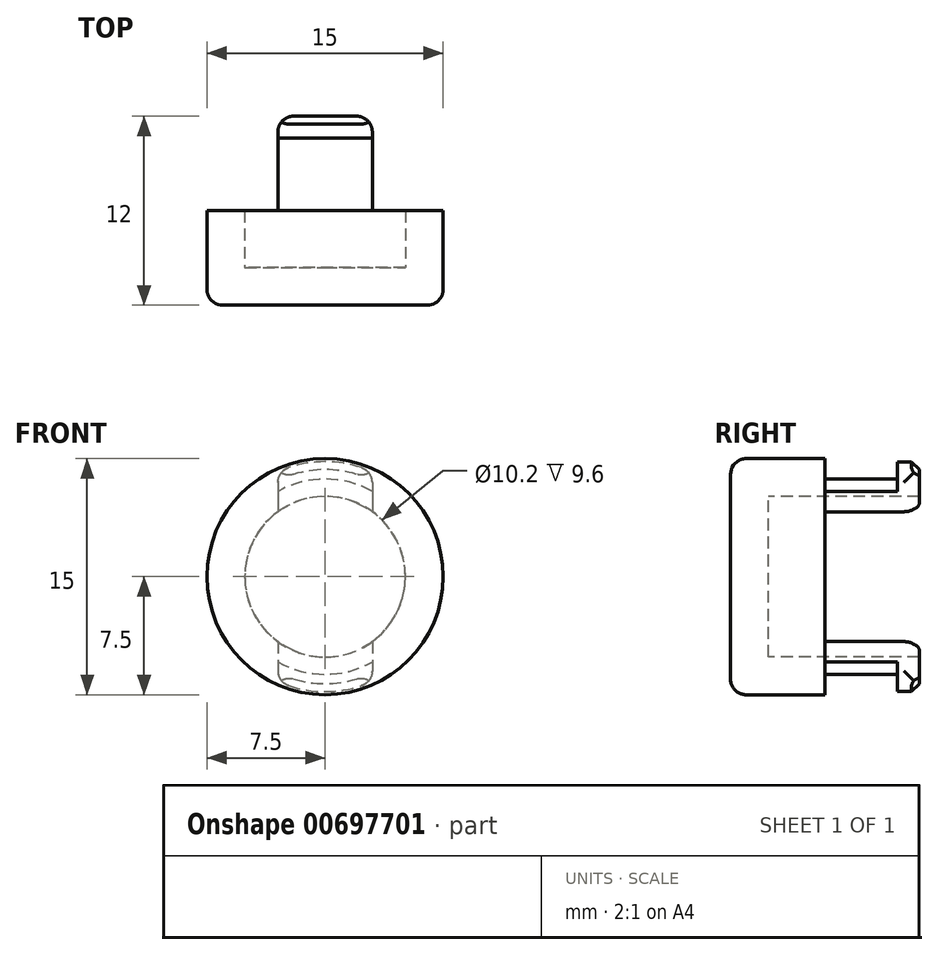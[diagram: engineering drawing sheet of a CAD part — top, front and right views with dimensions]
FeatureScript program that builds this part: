
annotation { "Feature Type Name" : "Feature", "Feature Type Description" : "" }
export const myFeature = defineFeature(function(context is Context, id is Id, definition is map)
    precondition{}
    {
        {
            var Q0;
            Q0=qCreatedBy(makeId("Front.planeOp"),FACE);
            cPlane(context, id + "F0", {"entities" : qUnion([Q0]), "cplaneType" : CPlaneType.OFFSET, "offset" : 13 * mm, "width" : 150 * mm, "height" : 150 * mm});
        }
        {
            var Q0;
            Q0=qCreatedBy(id+"F0.planeOp",FACE);
            var sketch = newSketch(context, id + "F1", { "sketchPlane" : qUnion([Q0])});
            skCircle(sketch, "E0", {"center": v(-13, 13) * mm, "radius": 7.5 * mm});
            skSolve(sketch);
        }
        {
            var Q0;
            Q0 = qSketchRegion(id + "F1", true);
            extrude(context, id + "F2", {"entities" : qUnion([Q0]), "oppositeDirection" : true, "depth" : 6 * mm, "offsetDistance" : 25 * mm});
        }
        {
            var Q0;
            Q0=makeQuery(id+"F2.opExtrude","CAP_EDGE",EDGE,{"disambiguationData":[OSD([sQuery(id+"F1.wireOp",EDGE,"E0")])],"isStart":true});
            fillet(context, id + "F3", {"entities" : qUnion([Q0]), "radius" : 1 * mm, "tangentPropagation" : true, "allowEdgeOverflow" : false});
        }
        {
            var Q0;
            Q0=makeQuery(id+"F2.opExtrude","CAP_FACE",FACE,{"disambiguationData":[OSD([sQuery(id+"F1.wireOp",EDGE,"E0")])],"isStart":false});
            shell(context, id + "F4", {"entities" : qUnion([Q0]), "thickness" : 2.4 * mm});
        }
        {
            var Q0;
            Q0=qCreatedBy(makeId("Front.planeOp"),FACE);
            cPlane(context, id + "F5", {"entities" : qUnion([Q0]), "cplaneType" : CPlaneType.OFFSET, "offset" : 2.4 * mm, "width" : 150 * mm, "height" : 150 * mm});
        }
        {
            var Q0;
            Q0=qCreatedBy(id+"F5.planeOp",FACE);
            var sketch = newSketch(context, id + "F6", { "sketchPlane" : qUnion([Q0])});
            skLineSegment(sketch, "E1.left", {"start": v(-10, 18.43) * mm, "end": v(-10, 17.12) * mm});
            skLineSegment(sketch, "E1.right", {"start": v(-16, 18.43) * mm, "end": v(-16, 17.12) * mm});
            skLineSegment(sketch, "E2.trimOffspring", {"start": v(-16, 8.88) * mm, "end": v(-16, 7.57) * mm});
            skLineSegment(sketch, "E3.trimOffspring", {"start": v(-10, 8.88) * mm, "end": v(-10, 7.57) * mm});
            skCircle(sketch, "E4.0.0", {"center": v(-13, 13) * mm, "radius": 5.1 * mm, "construction": true});
            skArc(sketch, "E5", {"start": v(-16, 7.57) * mm, "mid": v(-13, 6.8) * mm, "end": v(-10, 7.57) * mm});
            skArc(sketch, "E6", {"start": v(-16, 8.88) * mm, "mid": v(-13, 7.9) * mm, "end": v(-10, 8.88) * mm});
            skArc(sketch, "E7.trimOffspring", {"start": v(-10, 17.12) * mm, "mid": v(-13, 18.1) * mm, "end": v(-16, 17.12) * mm});
            skArc(sketch, "E8.trimOffspring", {"start": v(-10, 18.43) * mm, "mid": v(-13, 19.2) * mm, "end": v(-16, 18.43) * mm});
            skSolve(sketch);
        }
        {
            var Q0;
            Q0 = qSketchRegion(id + "F6", true);
            extrude(context, id + "F7", {"entities" : qUnion([Q0]), "operationType" : NewBodyOperationType.ADD, "endBound" : BoundingType.UP_TO_NEXT, "depth" : 25 * mm, "offsetDistance" : 25 * mm});
        }
        {
            var Q0;
            Q0=qCreatedBy(id+"F5.planeOp",FACE);
            var sketch = newSketch(context, id + "F8", { "sketchPlane" : qUnion([Q0])});
            skArc(sketch, "E9.0.0", {"start": v(-16, 17.12) * mm, "mid": v(-13, 7.9) * mm, "end": v(-10, 17.12) * mm, "construction": true});
            skArc(sketch, "E10", {"start": v(-16, 6.34) * mm, "mid": v(-13, 5.7) * mm, "end": v(-10, 6.34) * mm});
            skLineSegment(sketch, "E11.left", {"start": v(-10, 19.66) * mm, "end": v(-10, 17.12) * mm});
            skLineSegment(sketch, "E11.right", {"start": v(-16, 19.66) * mm, "end": v(-16, 17.12) * mm});
            skArc(sketch, "E12.trimOffspring", {"start": v(-10, 19.66) * mm, "mid": v(-13, 20.3) * mm, "end": v(-16, 19.66) * mm});
            skArc(sketch, "E13.trimOffspring", {"start": v(-10, 17.12) * mm, "mid": v(-13, 18.1) * mm, "end": v(-16, 17.12) * mm, "construction": true});
            skLineSegment(sketch, "E14.trimOffspring", {"start": v(-10, 8.88) * mm, "end": v(-10, 6.34) * mm});
            skLineSegment(sketch, "E15.trimOffspring", {"start": v(-16, 8.88) * mm, "end": v(-16, 6.34) * mm});
            skArc(sketch, "E16", {"start": v(-16, 8.88) * mm, "mid": v(-13, 7.9) * mm, "end": v(-10, 8.88) * mm});
            skArc(sketch, "E17.trimOffspring", {"start": v(-10, 17.12) * mm, "mid": v(-13, 18.1) * mm, "end": v(-16, 17.12) * mm});
            skSolve(sketch);
        }
        {
            var Q0;
            Q0 = qSketchRegion(id + "F8", true);
            extrude(context, id + "F9", {"entities" : qUnion([Q0]), "operationType" : NewBodyOperationType.ADD, "oppositeDirection" : true, "depth" : (1.7 - 0.3) * mm, "offsetDistance" : 25 * mm});
        }
        {
            var Q0;
            Q0=makeQuery(id+"F9.opExtrude","CAP_EDGE",EDGE,{"disambiguationData":[OSD([sQuery(id+"F8.wireOp",EDGE,"E10")])],"isStart":false});
            var Q1;
            Q1=makeQuery(id+"F9.opExtrude","CAP_EDGE",EDGE,{"disambiguationData":[OSD([sQuery(id+"F8.wireOp",EDGE,"E12.trimOffspring")])],"isStart":false});
            chamfer(context, id + "F10", {"entities" : qUnion([Q0, Q1]), "width" : 0.5 * mm, "tangentPropagation" : true});
        }
        {
            var Q0;
            Q0=makeQuery(id+"F9.opExtrude","SWEPT_EDGE",EDGE,{"disambiguationData":[OSD([sQuery(id+"F8.wireOp",EDGE,"E11.left"),sQuery(id+"F8.wireOp",EDGE,"E12.trimOffspring")])]});
            var Q1;
            Q1=makeQuery(id+"F9.opExtrude","SWEPT_EDGE",EDGE,{"disambiguationData":[OSD([sQuery(id+"F8.wireOp",EDGE,"E11.right"),sQuery(id+"F8.wireOp",EDGE,"E12.trimOffspring")])]});
            var Q2;
            Q2=makeQuery(id+"F9.opExtrude","SWEPT_EDGE",EDGE,{"disambiguationData":[OSD([sQuery(id+"F8.wireOp",EDGE,"E10"),sQuery(id+"F8.wireOp",EDGE,"E14.trimOffspring")])]});
            var Q3;
            Q3=makeQuery(id+"F9.opExtrude","SWEPT_EDGE",EDGE,{"disambiguationData":[OSD([sQuery(id+"F8.wireOp",EDGE,"E10"),sQuery(id+"F8.wireOp",EDGE,"E15.trimOffspring")])]});
            var Q4;
            Q4=makeQuery(id+"F9.opExtrude","CAP_EDGE",EDGE,{"disambiguationData":[OSD([sQuery(id+"F8.wireOp",EDGE,"E11.left")])],"isStart":false});
            var Q5;
            Q5=makeQuery(id+"F9.opExtrude","CAP_EDGE",EDGE,{"disambiguationData":[OSD([sQuery(id+"F8.wireOp",EDGE,"E11.right")])],"isStart":false});
            var Q6;
            Q6=makeQuery(id+"F9.opExtrude","CAP_EDGE",EDGE,{"disambiguationData":[OSD([sQuery(id+"F8.wireOp",EDGE,"E15.trimOffspring")])],"isStart":false});
            var Q7;
            Q7=makeQuery(id+"F9.opExtrude","CAP_EDGE",EDGE,{"disambiguationData":[OSD([sQuery(id+"F8.wireOp",EDGE,"E14.trimOffspring")])],"isStart":false});
            fillet(context, id + "F11", {"entities" : qUnion([Q0, Q1, Q2, Q3, Q4, Q5, Q6, Q7]), "radius" : 1 * mm, "tangentPropagation" : true, "allowEdgeOverflow" : false});
        }
    });
